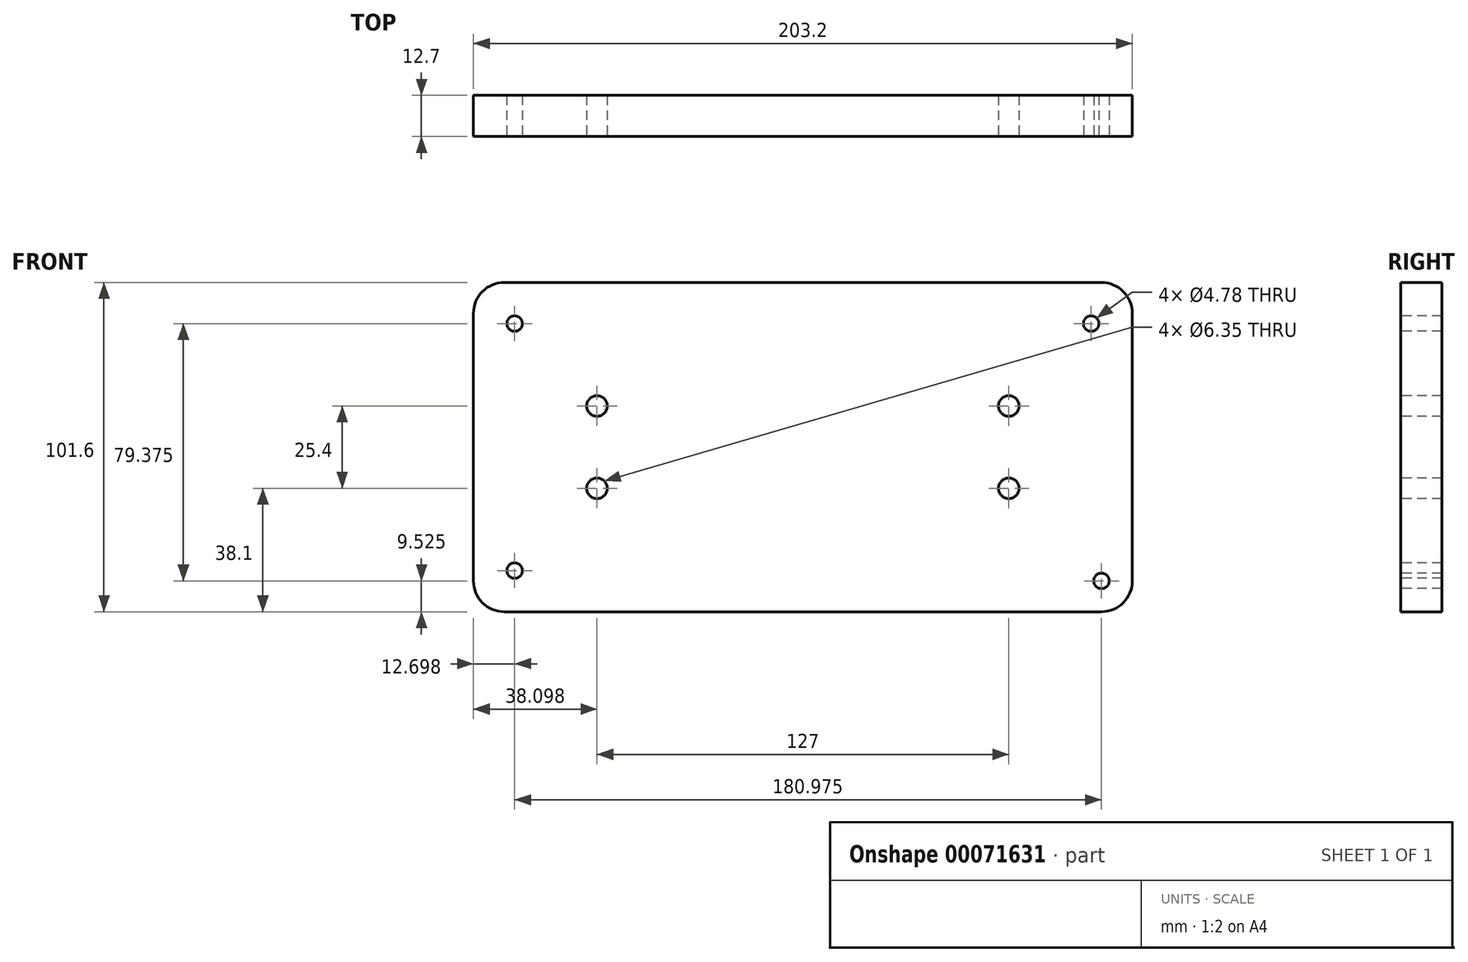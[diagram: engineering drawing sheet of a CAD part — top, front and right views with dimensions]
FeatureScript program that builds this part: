
annotation { "Feature Type Name" : "Feature", "Feature Type Description" : "" }
export const myFeature = defineFeature(function(context is Context, id is Id, definition is map)
    precondition{}
    {
        {
            var Q0;
            Q0=qCreatedBy(makeId("Front.planeOp"),FACE);
            var sketch = newSketch(context, id + "F0", { "sketchPlane" : qUnion([Q0])});
            skLineSegment(sketch, "E0.bottom", {"start": v(-93.13, 32.67) * mm, "end": v(110.07, 32.67) * mm});
            skLineSegment(sketch, "E0.top", {"start": v(-93.13, -68.93) * mm, "end": v(110.07, -68.93) * mm});
            skLineSegment(sketch, "E0.left", {"start": v(-93.13, 32.67) * mm, "end": v(-93.13, -68.93) * mm});
            skLineSegment(sketch, "E0.right", {"start": v(110.07, 32.67) * mm, "end": v(110.07, -68.93) * mm});
            skSolve(sketch);
        }
        {
            var Q0;
            Q0 = qSketchRegion(id + "F0", true);
            extrude(context, id + "F1", {"entities" : qUnion([Q0]), "depth" : 12.7 * mm});
        }
        {
            var Q0;
            Q0=makeQuery(id+"F1.opExtrude","SWEPT_EDGE",EDGE,{"disambiguationData":[OSD([sQuery(id+"F0.wireOp",EDGE,"E0.bottom"),sQuery(id+"F0.wireOp",EDGE,"E0.left")])]});
            var Q1;
            Q1=makeQuery(id+"F1.opExtrude","SWEPT_EDGE",EDGE,{"disambiguationData":[OSD([sQuery(id+"F0.wireOp",EDGE,"E0.top"),sQuery(id+"F0.wireOp",EDGE,"E0.left")])]});
            var Q2;
            Q2=makeQuery(id+"F1.opExtrude","SWEPT_EDGE",EDGE,{"disambiguationData":[OSD([sQuery(id+"F0.wireOp",EDGE,"E0.top"),sQuery(id+"F0.wireOp",EDGE,"E0.right")])]});
            var Q3;
            Q3=makeQuery(id+"F1.opExtrude","SWEPT_EDGE",EDGE,{"disambiguationData":[OSD([sQuery(id+"F0.wireOp",EDGE,"E0.bottom"),sQuery(id+"F0.wireOp",EDGE,"E0.right")])]});
            fillet(context, id + "F2", {"entities" : qUnion([Q0, Q1, Q2, Q3]), "radius" : 9.52 * mm, "tangentPropagation" : true, "allowEdgeOverflow" : false});
        }
        {
            var Q0;
            Q0=makeQuery(id+"F1.opExtrude","CAP_FACE",FACE,{"disambiguationData":[OSD([sQuery(id+"F0.wireOp",EDGE,"E0.bottom"),sQuery(id+"F0.wireOp",EDGE,"E0.top"),sQuery(id+"F0.wireOp",EDGE,"E0.left"),sQuery(id+"F0.wireOp",EDGE,"E0.right")])],"isStart":false});
            var sketch = newSketch(context, id + "F3", { "sketchPlane" : qUnion([Q0])});
            skPoint(sketch, "E1", {"position": v(-80.43, 19.97) * mm});
            skPoint(sketch, "E2", {"position": v(-80.43, -56.23) * mm});
            skPoint(sketch, "E3", {"position": v(100.54, -59.4) * mm});
            skPoint(sketch, "E4", {"position": v(97.37, -56.23) * mm});
            skPoint(sketch, "E5", {"position": v(97.37, 19.97) * mm});
            skSolve(sketch);
        }
        {
            var Q0;
            Q0=sQuery(id+"F3.wireOp",VERTEX,"E1");
            var Q1;
            Q1=sQuery(id+"F3.wireOp",VERTEX,"E2");
            var Q2;
            Q2=sQuery(id+"F3.wireOp",VERTEX,"E5");
            var Q3;
            Q3=sQuery(id+"F3.wireOp",VERTEX,"E3");
            var Q4;
            Q4=makeQuery(id+"F1.opExtrude","SWEPT_BODY",BODY,{"disambiguationData":[OSD([sQuery(id+"F0.wireOp",EDGE,"E0.bottom"),sQuery(id+"F0.wireOp",EDGE,"E0.top"),sQuery(id+"F0.wireOp",EDGE,"E0.left"),sQuery(id+"F0.wireOp",EDGE,"E0.right")])]});
            hole(context, id + "F4", {"style" : HoleStyle.SIMPLE, "holeDiameter" : 4.78 * mm, "endStyle" : HoleEndStyle.THROUGH, "locations" : qUnion([Q0, Q1, Q2, Q3]), "scope" : qUnion([Q4])});
        }
        {
            var Q0;
            Q0=makeQuery(id+"F1.opExtrude","CAP_FACE",FACE,{"disambiguationData":[OSD([sQuery(id+"F0.wireOp",EDGE,"E0.bottom"),sQuery(id+"F0.wireOp",EDGE,"E0.top"),sQuery(id+"F0.wireOp",EDGE,"E0.left"),sQuery(id+"F0.wireOp",EDGE,"E0.right")])],"isStart":false});
            var sketch = newSketch(context, id + "F5", { "sketchPlane" : qUnion([Q0])});
            skPoint(sketch, "E6", {"position": v(-55.03, -5.43) * mm});
            skPoint(sketch, "E7", {"position": v(-55.03, -30.83) * mm});
            skPoint(sketch, "E8", {"position": v(71.97, -5.43) * mm});
            skPoint(sketch, "E9", {"position": v(71.97, -30.83) * mm});
            skSolve(sketch);
        }
        {
            var Q0;
            Q0=sQuery(id+"F5.wireOp",VERTEX,"E6");
            var Q1;
            Q1=sQuery(id+"F5.wireOp",VERTEX,"E7");
            var Q2;
            Q2=sQuery(id+"F5.wireOp",VERTEX,"E8");
            var Q3;
            Q3=sQuery(id+"F5.wireOp",VERTEX,"E9");
            var Q4;
            Q4=makeQuery(id+"F1.opExtrude","SWEPT_BODY",BODY,{"disambiguationData":[OSD([sQuery(id+"F0.wireOp",EDGE,"E0.bottom"),sQuery(id+"F0.wireOp",EDGE,"E0.top"),sQuery(id+"F0.wireOp",EDGE,"E0.left"),sQuery(id+"F0.wireOp",EDGE,"E0.right")])]});
            hole(context, id + "F6", {"style" : HoleStyle.SIMPLE, "holeDiameter" : 6.35 * mm, "endStyle" : HoleEndStyle.THROUGH, "locations" : qUnion([Q0, Q1, Q2, Q3]), "scope" : qUnion([Q4])});
        }
    });
